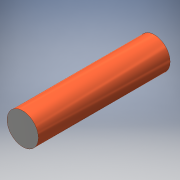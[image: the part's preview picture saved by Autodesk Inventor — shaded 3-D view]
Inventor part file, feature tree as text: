
AUTODESK INVENTOR PART (.ipt)
format: ipt  version: 2016 (Build 200138000, 138)  size: 100,864 bytes
history: native  units: mm
features: extrude x2, sketch x2
ambient origin geometry x8: Origin, YZ Plane, XZ Plane, XY Plane, X Axis, Y Axis, Z Axis, Center Point
bodies: Solid1 (feature_tree)
feature tree (4):
  extrude  "Extrusion1"  Depth=43.16mm TaperAngle=0.0deg
  extrude  "Extrusion2"  Depth=0.93mm TaperAngle=0.0deg
  sketch  "Sketch1"  dims[d0=10.26mm d1=43.16mm d2=0.0mm]
  sketch  "Sketch2"  dims[d3=3.5mm d4=0.93mm d5=0.0mm]
